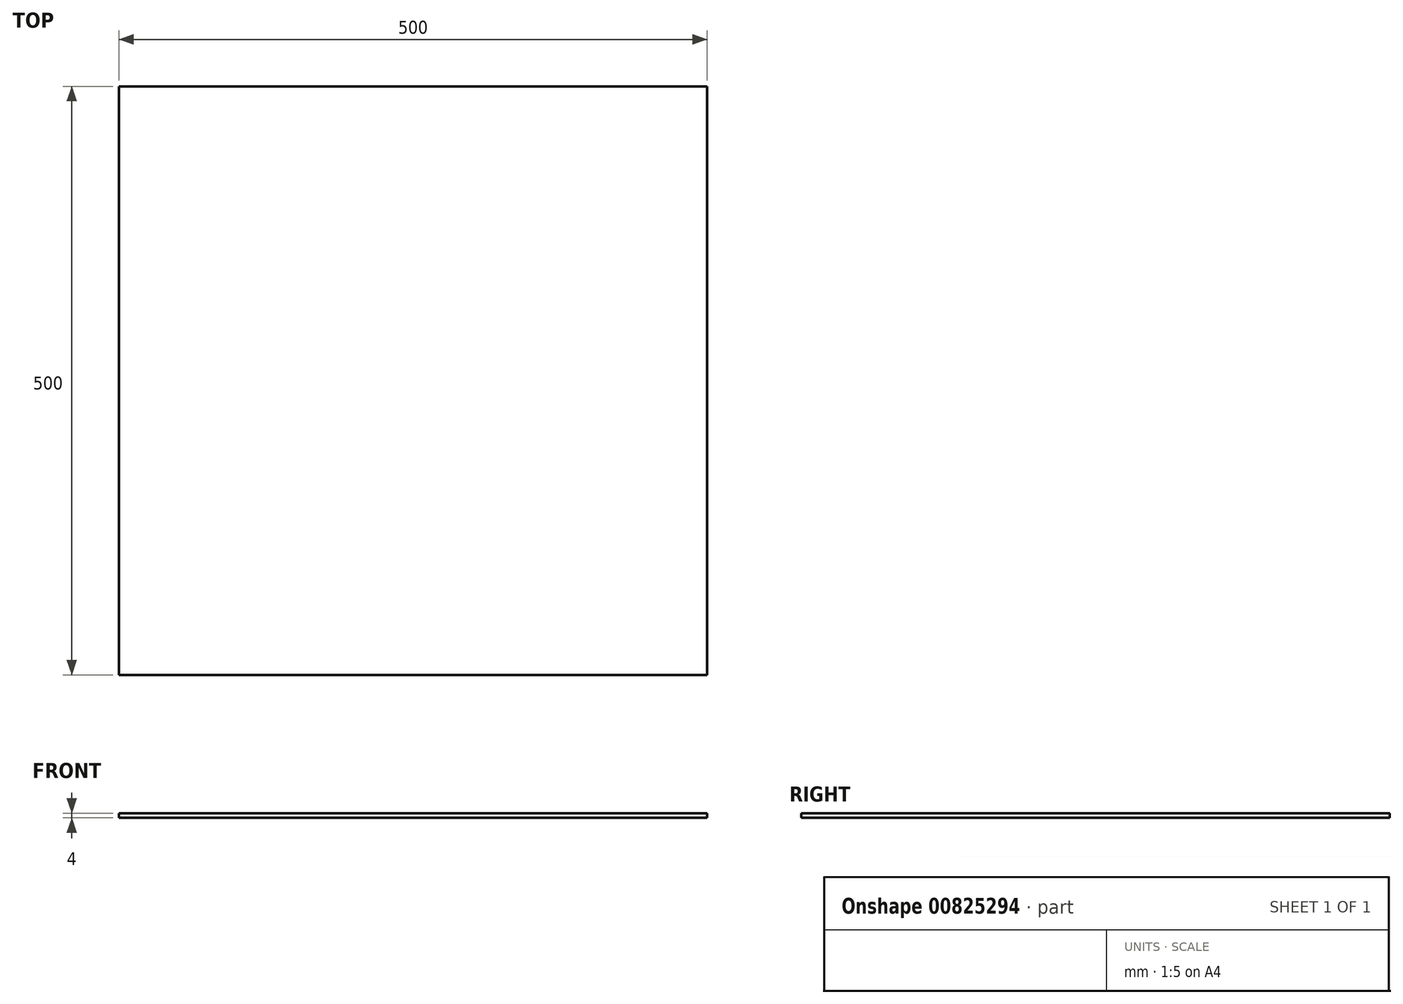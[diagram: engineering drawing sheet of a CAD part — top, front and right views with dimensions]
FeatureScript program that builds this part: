
annotation { "Feature Type Name" : "Feature", "Feature Type Description" : "" }
export const myFeature = defineFeature(function(context is Context, id is Id, definition is map)
    precondition{}
    {
        {
            assignVariable(context, id + "F0", {"name" : "glass_W", "anyValue" : 4});
        }
        {
            var Q0;
            Q0=qCreatedBy(makeId("Top.planeOp"),FACE);
            var sketch = newSketch(context, id + "F1", { "sketchPlane" : qUnion([Q0])});
            skLineSegment(sketch, "E0.bottom", {"start": v(-250, 250) * mm, "end": v(250, 250) * mm});
            skLineSegment(sketch, "E0.top", {"start": v(-250, -250) * mm, "end": v(250, -250) * mm});
            skLineSegment(sketch, "E0.left", {"start": v(-250, 250) * mm, "end": v(-250, -250) * mm});
            skLineSegment(sketch, "E0.right", {"start": v(250, 250) * mm, "end": v(250, -250) * mm});
            skPoint(sketch, "E0.middle", {"position": v(0, 0) * mm});
            skSolve(sketch);
        }
        {
            var Q0;
            Q0=makeQuery(id+"F1.imprint","IMPRINT",FACE,{"disambiguationData":[TD([[makeQuery(id+"F1.imprint","IMPRINT",EDGE,{"derivedFrom":sQuery(id+"F1.wireOp",EDGE,"E0.bottom")}),-1.0]])]});
            extrude(context, id + "F2", {"entities" : qUnion([Q0]), "depth" : (getVariable(context, 'glass_W')) * mm, "offsetDistance" : 25 * mm});
        }
    });
